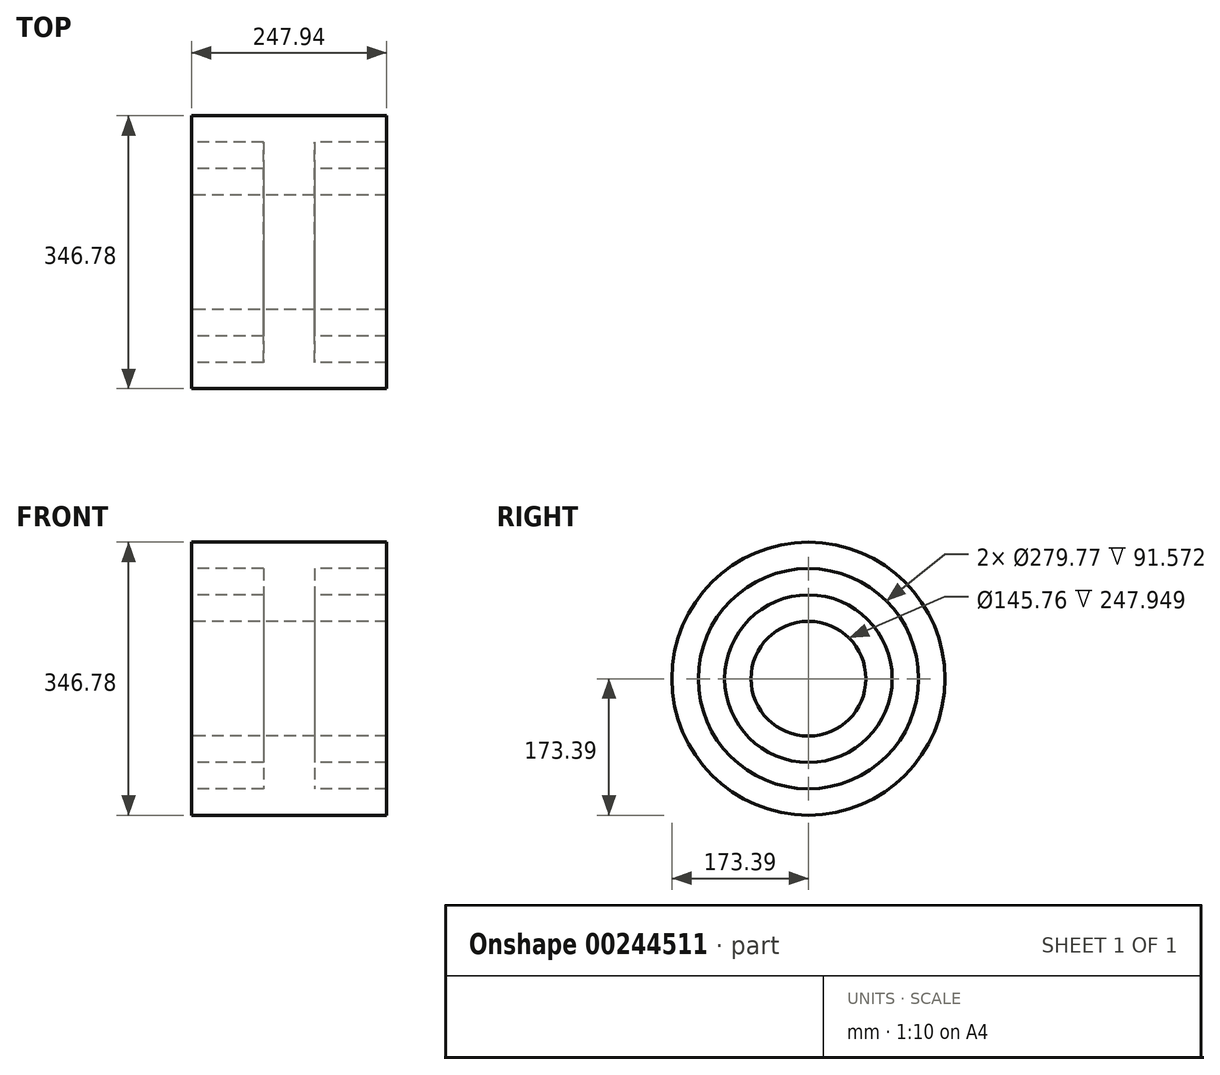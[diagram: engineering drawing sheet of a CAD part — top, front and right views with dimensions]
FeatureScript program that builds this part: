
annotation { "Feature Type Name" : "Feature", "Feature Type Description" : "" }
export const myFeature = defineFeature(function(context is Context, id is Id, definition is map)
    precondition{}
    {
        {
            var Q0;
            Q0=qCreatedBy(makeId("Front.planeOp"),FACE);
            var sketch = newSketch(context, id + "F0", { "sketchPlane" : qUnion([Q0])});
            skPoint(sketch, "E0.middle", {"position": v(0, 0) * mm});
            skLineSegment(sketch, "E1", {"start": v(-92.09, 0) * mm, "end": v(96.02, 0) * mm, "construction": true});
            skLineSegment(sketch, "E2", {"start": v(0, 263.2) * mm, "end": v(0, 0) * mm, "construction": true});
            skLineSegment(sketch, "E3", {"start": v(0, 173.39) * mm, "end": v(123.97, 173.39) * mm});
            skLineSegment(sketch, "E4", {"start": v(123.97, 173.39) * mm, "end": v(123.97, 139.88) * mm});
            skLineSegment(sketch, "E5", {"start": v(123.97, 139.88) * mm, "end": v(32.4, 139.88) * mm});
            skLineSegment(sketch, "E6", {"start": v(32.4, 139.88) * mm, "end": v(32.4, 106.38) * mm});
            skLineSegment(sketch, "E7", {"start": v(32.4, 106.38) * mm, "end": v(123.97, 106.38) * mm});
            skLineSegment(sketch, "E8", {"start": v(123.97, 106.38) * mm, "end": v(123.97, 72.88) * mm});
            skLineSegment(sketch, "E9", {"start": v(123.97, 72.88) * mm, "end": v(0, 72.88) * mm});
            skLineSegment(sketch, "E10.MirrorCS", {"start": v(0, 173.39) * mm, "end": v(-123.97, 173.39) * mm});
            skLineSegment(sketch, "E11.MirrorCS", {"start": v(-123.97, 173.39) * mm, "end": v(-123.97, 139.88) * mm});
            skLineSegment(sketch, "E12.MirrorCS", {"start": v(-123.97, 139.88) * mm, "end": v(-32.4, 139.88) * mm});
            skLineSegment(sketch, "E13.MirrorCS", {"start": v(-32.4, 139.88) * mm, "end": v(-32.4, 106.38) * mm});
            skLineSegment(sketch, "E14.MirrorCS", {"start": v(-32.4, 106.38) * mm, "end": v(-123.97, 106.38) * mm});
            skLineSegment(sketch, "E15.MirrorCS", {"start": v(-123.97, 106.38) * mm, "end": v(-123.97, 72.88) * mm});
            skLineSegment(sketch, "E16.MirrorCS", {"start": v(-123.97, 72.88) * mm, "end": v(0, 72.88) * mm});
            skSolve(sketch);
        }
        {
            var Q0;
            Q0 = qSketchRegion(id + "F0", true);
            var Q1;
            Q1=sQuery(id+"F0.wireOp",EDGE,"E1");
            revolve(context, id + "F1", {"entities" : qUnion([Q0]), "axis" : qUnion([Q1]), "revolveType" : RevolveType.FULL});
        }
    });
